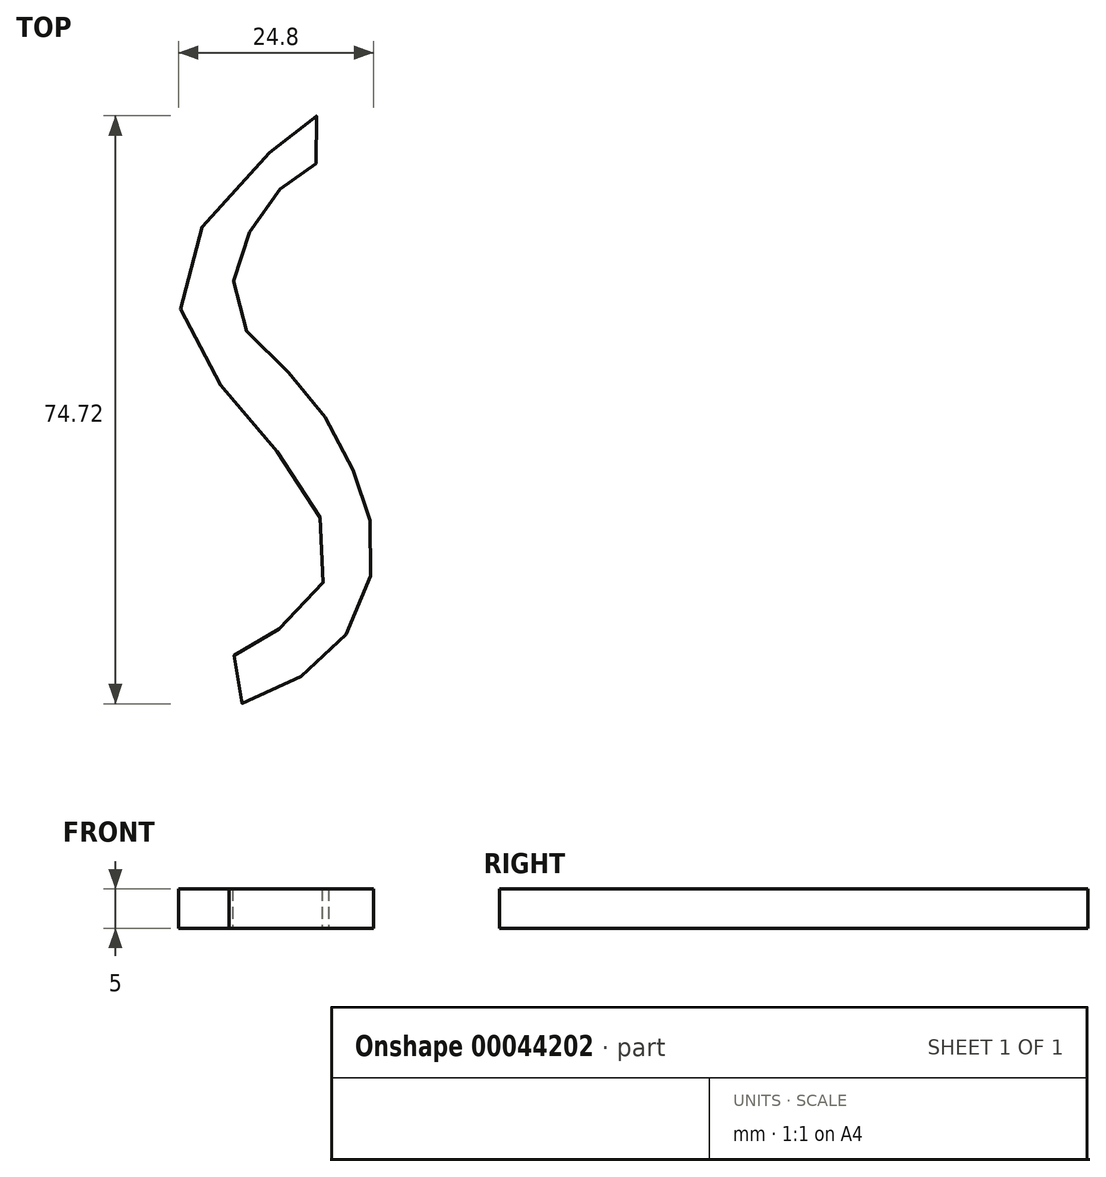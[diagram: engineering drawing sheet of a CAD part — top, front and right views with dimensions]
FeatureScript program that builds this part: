
annotation { "Feature Type Name" : "Feature", "Feature Type Description" : "" }
export const myFeature = defineFeature(function(context is Context, id is Id, definition is map)
    precondition{}
    {
        {
            var Q0;
            Q0=qCreatedBy(makeId("Top.planeOp"),FACE);
            var sketch = newSketch(context, id + "F0", { "sketchPlane" : qUnion([Q0])});
            skFitSpline(sketch, "E0", {"points": [v(-36.04, 59.03) * mm, v(-39.53, 56.61) * mm, v(-43.57, 52.04) * mm, v(-45.99, 46.4) * mm, v(-46.26, 40.2) * mm, v(-41.42, 34.3) * mm, v(-36.3, 28.91) * mm, v(-32, 21.65) * mm, v(-29.58, 15.2) * mm, v(-28.78, 8.74) * mm, v(-31.74, 0) * mm, v(-37.92, -6.05) * mm, v(-45.99, -9.28) * mm, v(-46.26, -3.1) * mm, v(-40.61, 0) * mm, v(-34.7, 7.13) * mm, v(-37.38, 17.62) * mm, v(-47.87, 30.52) * mm, v(-53.25, 45.32) * mm, v(-40.34, 62) * mm, v(-35.77, 64.95) * mm, v(-36.04, 59.03) * mm]});
            skSolve(sketch);
        }
        {
            var Q0;
            Q0=makeQuery(id+"F0.imprint","IMPRINT",FACE,{"disambiguationData":[TD([[makeQuery(id+"F0.imprint","IMPRINT",EDGE,{"derivedFrom":sQuery(id+"F0.wireOp",EDGE,"E0")}),-1.0]])]});
            extrude(context, id + "F1", {"entities" : qUnion([Q0]), "depth" : 5 * mm});
        }
    });
